# Revit family: VENTS-VNV_1_80_KP
name_source: partatom
category: Mechanical Equipment
units: mm (PartAtom-declared; Revit-internal decimal feet)

## family parameters
Always vertical = No
Classification = None
Cut with Voids When Loaded = No
OmniClass Number = 23.75.35.17
OmniClass Title = Fans
Part Type = Breaks Into
Room Calculation Point = No
Round Connector Dimension = Use Diameter
Shared = No
Work Plane-Based = No

## types (3) — shared parameters
CaseDepth = 135 mm  [stored 0.442913 ft]
CaseHeight = 266 mm  [stored 0.872703 ft]
CaseWidth = 266 mm  [stored 0.872703 ft]
CoverHeight = 274 mm  [stored 0.89895 ft]
CoverWidth = 274 mm  [stored 0.89895 ft]
Current = 0 A
Description = Centrifugal fan in fireproof casing
Duct Connection Size = 80 mm  [stored 0.262467 ft]
Family Version = 1.0
Fan Material = Plastic White Glazed
Load Classification = HVAC
Maintenance Zone Front = 600 mm  [stored 1.9685 ft]
Maintenance Zone Material = Maintenance Zone
Manufacturer = Vents
Max. Transported Air Temperature (°C) = +50
Metal Material = Metal Zinc
Model = VNV-1 80 KP
Number of Poles = 1
Power Factor = 1
Type Comments = Centrifugal fan in fireproof casing VNV-1 80 KP
URL = https://ventilation-system.com
Voltage = 230 V
Weight = 0.00 kg

## per-type parameters (varying)
| type | Apparent Power | Maximum Air Flow | Noise Level at 3 m (dBa) | Power | RPM (min-1) |
| VNV-1 80 KP (speed 1) | 17 VA | 63 m³/h | 30 | 17 W | 1350 |
| VNV-1 80 KP (speed 2) | 27 VA | 102 m³/h | 35.2 | 27 W | 1830 |
| VNV-1 80 KP (speed 3) | 48 VA | 150 m³/h | 43.7 | 48 W | 2640 |

note: [stored X ft] marks values corroborated as IEEE doubles in the binary element streams (Revit-internal decimal feet)

## geometry (parser evidence)
native form markers: Sweep x8
no freeform markers — native parametric forms only
